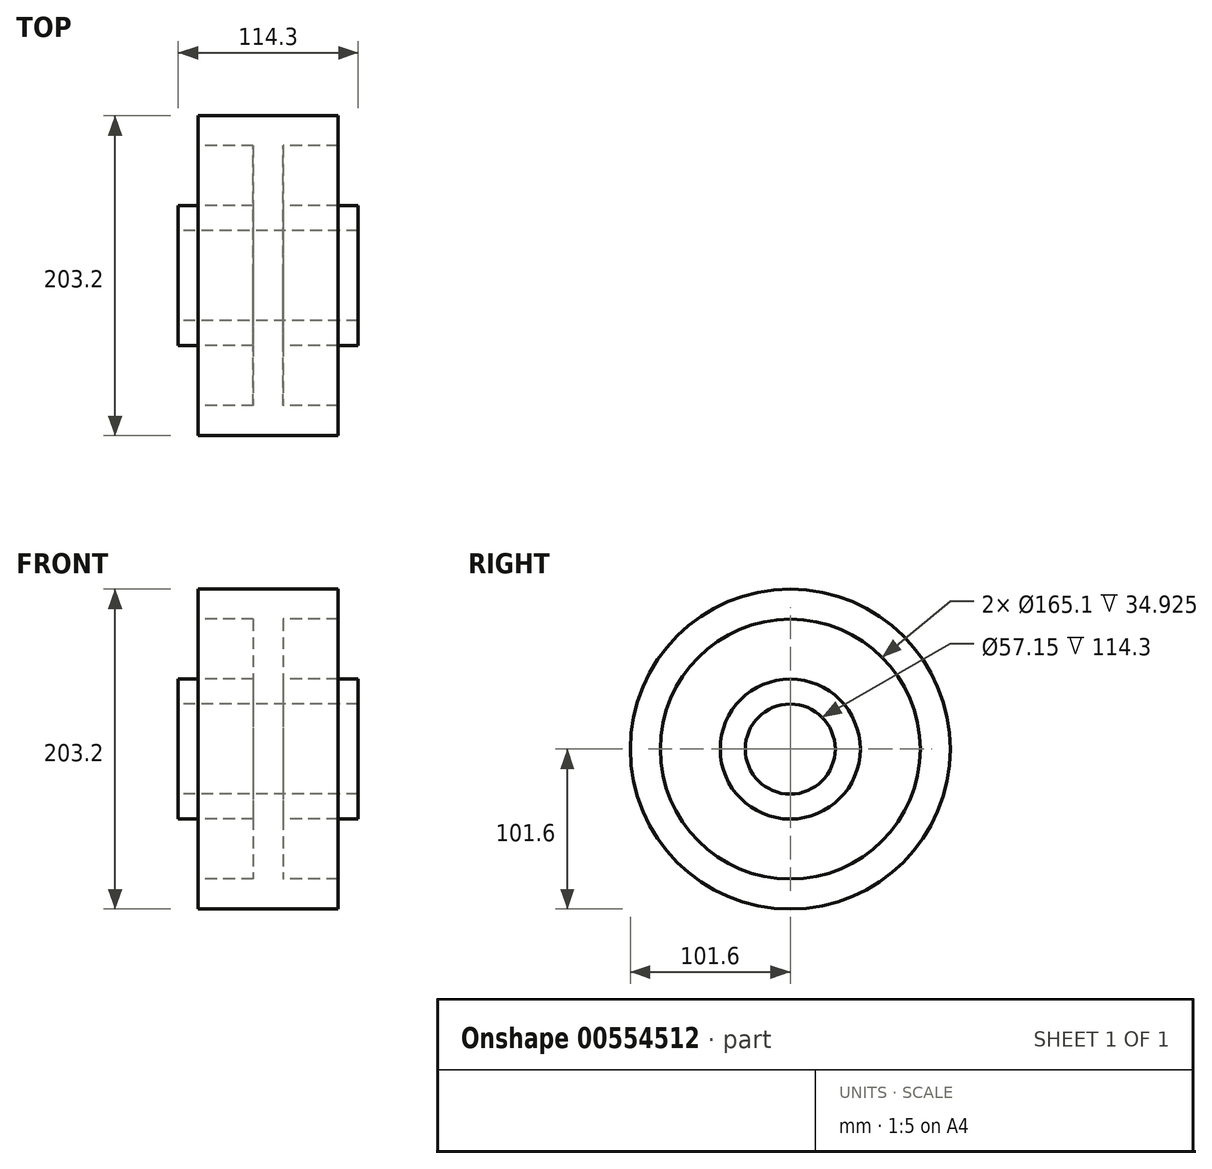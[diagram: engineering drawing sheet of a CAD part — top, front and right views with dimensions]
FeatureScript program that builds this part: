
annotation { "Feature Type Name" : "Feature", "Feature Type Description" : "" }
export const myFeature = defineFeature(function(context is Context, id is Id, definition is map)
    precondition{}
    {
        {
            var Q0;
            Q0=qCreatedBy(makeId("Front.planeOp"),FACE);
            var sketch = newSketch(context, id + "F0", { "sketchPlane" : qUnion([Q0])});
            skLineSegment(sketch, "E0", {"start": v(-183.48, 0) * mm, "end": v(200.51, 0) * mm, "construction": true});
            skLineSegment(sketch, "E1", {"start": v(-57.15, 28.57) * mm, "end": v(57.15, 28.58) * mm});
            skLineSegment(sketch, "E2", {"start": v(57.15, 28.58) * mm, "end": v(57.15, 44.45) * mm});
            skLineSegment(sketch, "E3", {"start": v(57.15, 44.45) * mm, "end": v(9.52, 44.45) * mm});
            skLineSegment(sketch, "E4", {"start": v(9.52, 44.45) * mm, "end": v(9.53, 82.55) * mm});
            skLineSegment(sketch, "E5", {"start": v(9.53, 82.55) * mm, "end": v(44.45, 82.55) * mm});
            skLineSegment(sketch, "E6", {"start": v(44.45, 82.55) * mm, "end": v(44.45, 101.6) * mm});
            skLineSegment(sketch, "E7", {"start": v(44.45, 101.6) * mm, "end": v(-44.45, 101.6) * mm});
            skLineSegment(sketch, "E8", {"start": v(-44.45, 101.6) * mm, "end": v(-44.45, 82.55) * mm});
            skLineSegment(sketch, "E9", {"start": v(-44.45, 82.55) * mm, "end": v(-9.53, 82.55) * mm});
            skLineSegment(sketch, "E10", {"start": v(-9.53, 82.55) * mm, "end": v(-9.52, 44.45) * mm});
            skLineSegment(sketch, "E11", {"start": v(-9.52, 44.45) * mm, "end": v(-57.15, 44.45) * mm});
            skLineSegment(sketch, "E12", {"start": v(-57.15, 44.45) * mm, "end": v(-57.15, 28.58) * mm});
            skLineSegment(sketch, "E13", {"start": v(0, 0) * mm, "end": v(0, 126.4) * mm, "construction": true});
            skSolve(sketch);
        }
        {
            var Q0;
            Q0 = qSketchRegion(id + "F0", true);
            var Q1;
            Q1=sQuery(id+"F0.wireOp",EDGE,"E0");
            revolve(context, id + "F1", {"entities" : qUnion([Q0]), "axis" : qUnion([Q1]), "revolveType" : RevolveType.FULL});
        }
    });
